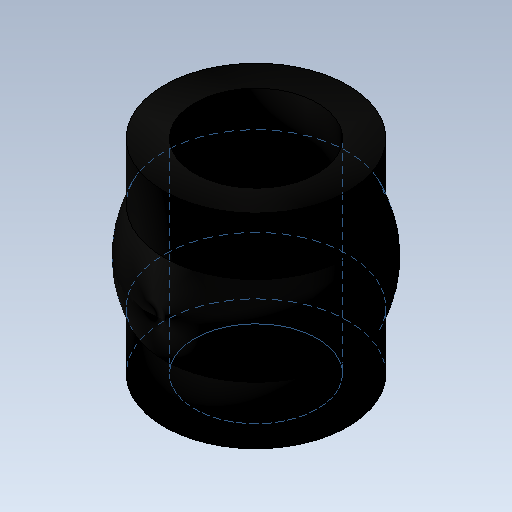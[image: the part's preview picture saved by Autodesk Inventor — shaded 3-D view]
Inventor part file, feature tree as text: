
AUTODESK INVENTOR PART (.ipt)
format: ipt  version: 2020 (Build 240168000, 168)  size: 138,752 bytes
history: native  units: mm
features: sketch x3, extrude x2, other x1, revolve x1
ambient origin geometry x8: Origin, YZ Plane, XZ Plane, XY Plane, X Axis, Y Axis, Z Axis, Center Point
bodies: Body1 (feature_tree)
feature tree (7):
  other  "ソリッド1"
  revolve  "回転1"
  extrude  "押し出し1"  Depth=2.5mm
  extrude  "押し出し2"  Depth=2.5mm
  sketch  "スケッチ1"
  sketch  "スケッチ2"
  sketch  "スケッチ3"
